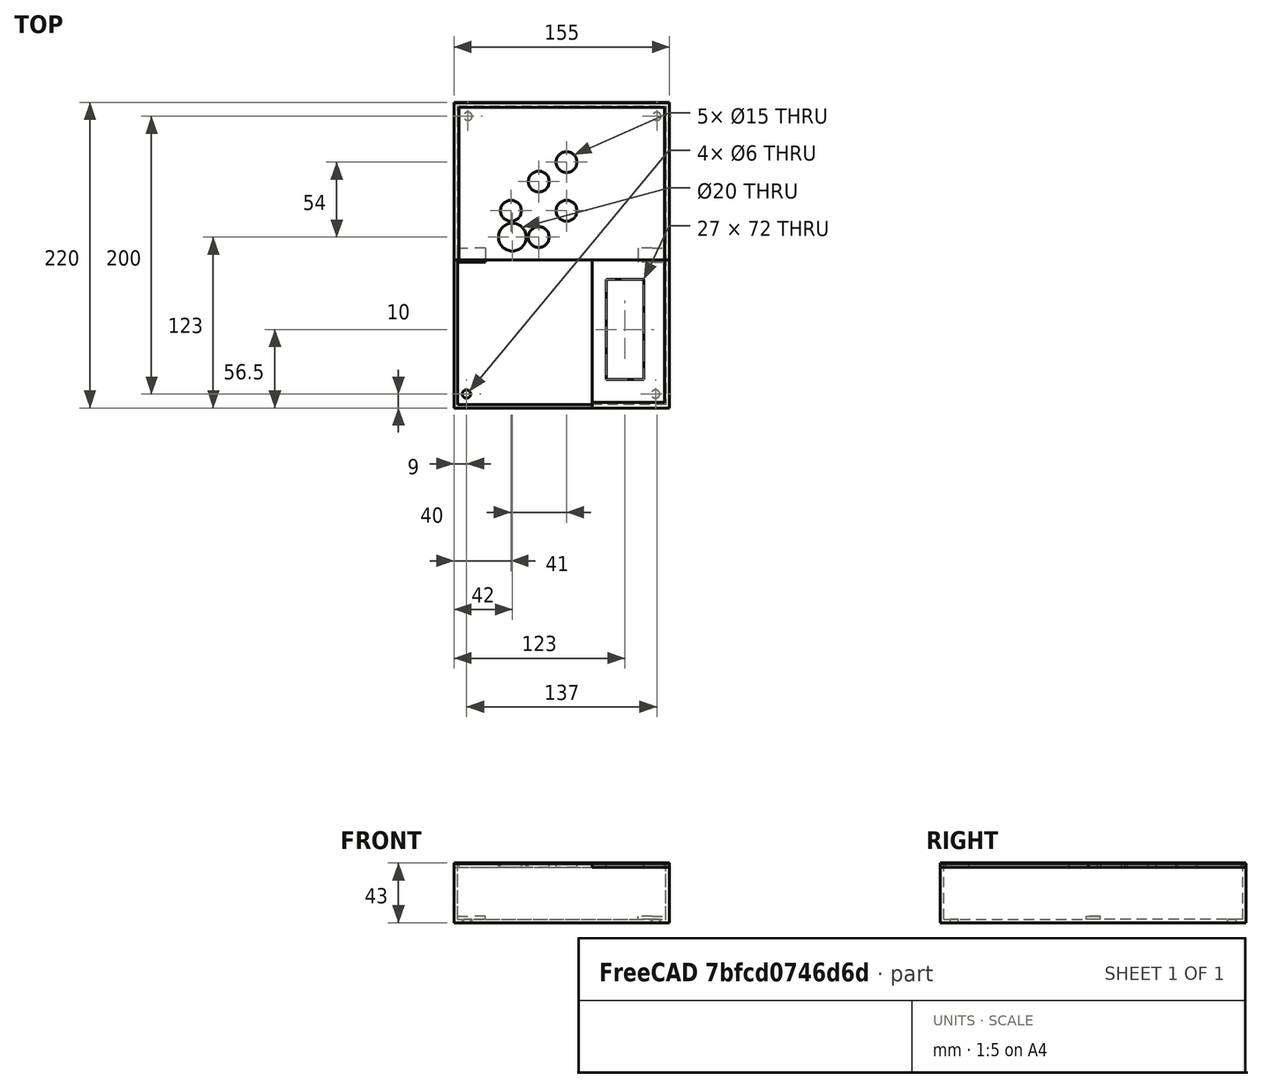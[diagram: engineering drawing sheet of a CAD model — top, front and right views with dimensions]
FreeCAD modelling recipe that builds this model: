
FCSTD DOCUMENT  (FreeCAD 0.17R13541 (Git))
Label: Todo
License: All rights reserved
LicenseURL: http://en.wikipedia.org/wiki/All_rights_reserved
objects: Part::Box×17, Part::Cut×12, Part::Cylinder×10, Part::MultiFuse×5, Part::Fuse×1
note: 45 computed .brp shape members not serialized (recipe doc carries the construction recipe); baked Part::Feature solids carry a one-line shape summary decoded from their .brp

FEATURE [Part::Box] Box004  label="base"
  AttacherType = Attacher::AttachEngine3D
  Height = 2.5
  Length = 155
  Width = 110
FEATURE [Part::Box] Box005  label="wall_lado1"
  AttacherType = Attacher::AttachEngine3D
  Height = 42.5
  Length = 2.5
  Width = 110
FEATURE [Part::Box] Box006  label="wall_lado2"
  AttacherType = Attacher::AttachEngine3D
  Height = 42.5
  Length = 2.5
  Placement = pos=(152.5,0,0) rot=(0,0,1;0rad)
  Width = 110
FEATURE [Part::Box] Box007  label="wall_tras"
  AttacherType = Attacher::AttachEngine3D
  Height = 42.5
  Length = 155
  Placement = pos=(0,107.5,0) rot=(0,0,1;0rad)
  Width = 2.5
FEATURE [Part::Cylinder] Cylinder001  label="buraco_1"
  Angle = 360
  AttacherType = Attacher::AttachEngine3D
  Height = 10
  Placement = pos=(10,100,0) rot=(0,0,1;0rad)
  Radius = 3
FEATURE [Part::Cylinder] Cylinder002  label="buraco_2"
  Angle = 360
  AttacherType = Attacher::AttachEngine3D
  Height = 10
  Placement = pos=(146,100,0) rot=(0,0,1;0rad)
  Radius = 3
FEATURE [Part::MultiFuse] Fusion001
  Shapes = -> [Box005,Box006,Box007,Box004]
FEATURE [Part::Cut] Cut
  Base = -> Fusion001
  Tool = -> Cylinder002
FEATURE [Part::Cut] Cut001
  Base = -> Cut
  Tool = -> Cylinder001
FEATURE [Part::Box] Box008  label="suporte1"
  AttacherType = Attacher::AttachEngine3D
  Height = 2
  Length = 10
  Placement = pos=(2.5,-5,2.5) rot=(0,0,1;0rad)
  Width = 10
FEATURE [Part::Box] Box009  label="suporte2"
  AttacherType = Attacher::AttachEngine3D
  Height = 2
  Length = 10
  Placement = pos=(142.5,-5,2.5) rot=(0,0,1;0rad)
  Width = 10
FEATURE [Part::MultiFuse] Fusion
  Shapes = -> [Box009,Cut001]
FEATURE [Part::MultiFuse] Fusion002  label="parte1"
  Shapes = -> [Box008,Fusion]
FEATURE [Part::Box] Box  label="tampa1"
  AttacherType = Attacher::AttachEngine3D
  Height = 3
  Length = 155
  Placement = pos=(0,-3.5,40) rot=(0,0,1;0rad)
  Width = 113
FEATURE [Part::Box] Box010  label="tampa2"
  AttacherType = Attacher::AttachEngine3D
  Height = 3
  Length = 55.5
  Placement = pos=(99.5,-110,40) rot=(0,0,1;0rad)
  Width = 106.5
FEATURE [Part::Box] Box011  label="base001"
  AttacherType = Attacher::AttachEngine3D
  Height = 2.5
  Length = 155
  Width = 110
FEATURE [Part::Box] Box012  label="wall_lado003"
  AttacherType = Attacher::AttachEngine3D
  Height = 42.5
  Length = 2.5
  Width = 110
FEATURE [Part::Box] Box013  label="wall_lado004"
  AttacherType = Attacher::AttachEngine3D
  Height = 42.5
  Length = 2.5
  Placement = pos=(152.5,0,0) rot=(0,0,1;0rad)
  Width = 110
FEATURE [Part::Box] Box014  label="suporte004"
  AttacherType = Attacher::AttachEngine3D
  Height = 2
  Length = 10
  Placement = pos=(12.5,-5,2.5) rot=(0,0,1;0rad)
  Width = 10
FEATURE [Part::Box] Box015  label="suporte003"
  AttacherType = Attacher::AttachEngine3D
  Height = 2
  Length = 10
  Placement = pos=(132.5,-5,2.5) rot=(0,0,1;0rad)
  Width = 10
FEATURE [Part::Cylinder] Cylinder003  label="buraco_003"
  Angle = 360
  AttacherType = Attacher::AttachEngine3D
  Height = 10
  Placement = pos=(10,100,0) rot=(0,0,1;0rad)
  Radius = 3
FEATURE [Part::Box] Box016  label="wall_tras001"
  AttacherType = Attacher::AttachEngine3D
  Height = 42.5
  Length = 155
  Placement = pos=(0,107.5,0) rot=(0,0,1;0rad)
  Width = 2.5
FEATURE [Part::MultiFuse] Fusion004
  Shapes = -> [Box012,Box013,Box016,Box011]
FEATURE [Part::Cylinder] Cylinder004  label="buraco_004"
  Angle = 360
  AttacherType = Attacher::AttachEngine3D
  Height = 10
  Placement = pos=(146,100,0) rot=(0,0,1;0rad)
  Radius = 3
FEATURE [Part::Cut] Cut002
  Base = -> Fusion004
  Tool = -> Cylinder004
FEATURE [Part::Cut] Cut003
  Base = -> Cut002
  Tool = -> Cylinder003
FEATURE [Part::MultiFuse] Fusion003  label="partedois"
  Placement = pos=(155,0,0) rot=(0,0,1;3.14159rad)
  Shapes = -> [Box014,Box015,Cut003]
FEATURE [Part::Fuse] Fusion005  label="Caixa"
  Base = -> Fusion002
  Tool = -> Fusion003
FEATURE [Part::Box] Box017  label="teclado"
  AttacherType = Attacher::AttachEngine3D
  Height = 3
  Length = 148
  Placement = pos=(3.5,-3.5,40) rot=(0,0,1;0rad)
  Width = 110
FEATURE [Part::Box] Box018  label="lcd"
  AttacherType = Attacher::AttachEngine3D
  Height = 3
  Length = 52
  Placement = pos=(99.5,-106,40) rot=(0,0,1;0rad)
  Width = 102.5
FEATURE [Part::Box] Box019  label="buraco"
  AttacherType = Attacher::AttachEngine3D
  Height = 3
  Length = 27
  Placement = pos=(109.5,-89.5,40) rot=(0,0,1;0rad)
  Width = 72
FEATURE [Part::Cylinder] Cylinder  label="botao1"
  Angle = 360
  AttacherType = Attacher::AttachEngine3D
  Height = 3
  Placement = pos=(41,32,40) rot=(0,0,1;0rad)
  Radius = 7.5
FEATURE [Part::Cylinder] Cylinder005  label="botao2"
  Angle = 360
  AttacherType = Attacher::AttachEngine3D
  Height = 3
  Placement = pos=(61,13,40) rot=(0,0,1;0rad)
  Radius = 7.5
FEATURE [Part::Cylinder] Cylinder006  label="botao3"
  Angle = 360
  AttacherType = Attacher::AttachEngine3D
  Height = 3
  Placement = pos=(61,53,40) rot=(0,0,1;0rad)
  Radius = 7.5
FEATURE [Part::Cylinder] Cylinder007  label="botao4"
  Angle = 360
  AttacherType = Attacher::AttachEngine3D
  Height = 3
  Placement = pos=(81,32,40) rot=(0,0,1;0rad)
  Radius = 7.5
FEATURE [Part::Cylinder] Cylinder008  label="botao5"
  Angle = 360
  AttacherType = Attacher::AttachEngine3D
  Height = 3
  Placement = pos=(81,67,40) rot=(0,0,1;0rad)
  Radius = 7.5
FEATURE [Part::Cylinder] Cylinder009  label="buzzer"
  Angle = 360
  AttacherType = Attacher::AttachEngine3D
  Height = 3
  Placement = pos=(42,13,40) rot=(0,0,1;0rad)
  Radius = 10
FEATURE [Part::Cut] Cut004  label="Moldura_LCD"
  Base = -> Box018
  Tool = -> Box019
FEATURE [Part::Cut] Cut005
  Base = -> Box017
  Tool = -> Cylinder
FEATURE [Part::Cut] Cut006
  Base = -> Cut005
  Tool = -> Cylinder008
FEATURE [Part::Cut] Cut007
  Base = -> Cut006
  Tool = -> Cylinder008
FEATURE [Part::Cut] Cut008
  Base = -> Cut007
  Tool = -> Cylinder007
FEATURE [Part::Cut] Cut009
  Base = -> Cut008
  Tool = -> Cylinder006
FEATURE [Part::Cut] Cut010
  Base = -> Cut009
  Tool = -> Cylinder005
FEATURE [Part::Cut] Cut011  label="Moldura_Teclado"
  Base = -> Cut010
  Tool = -> Cylinder009
